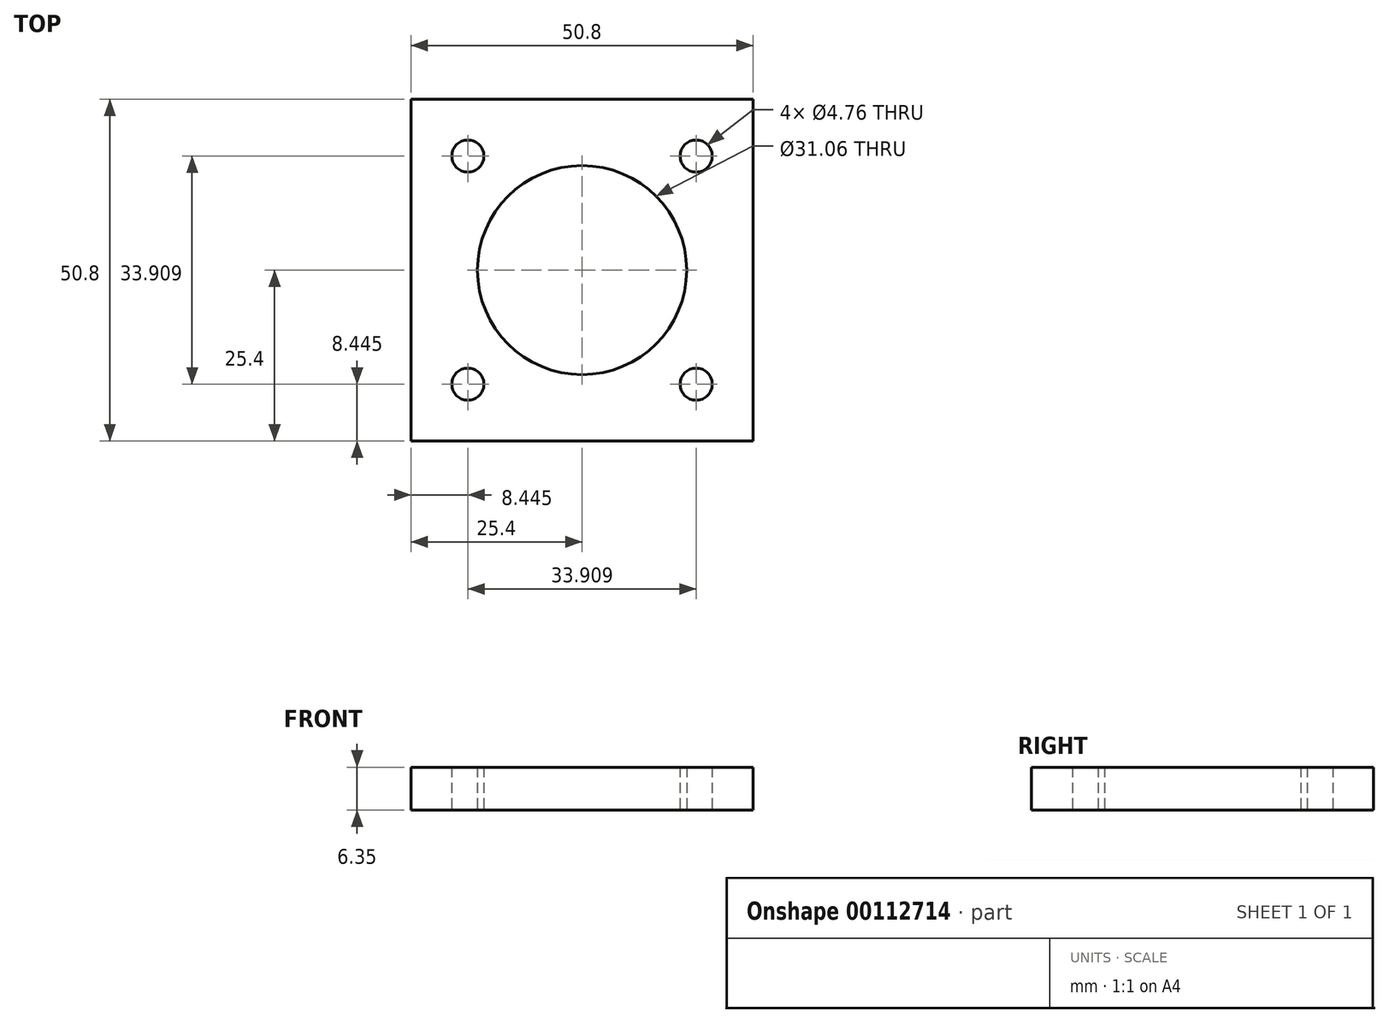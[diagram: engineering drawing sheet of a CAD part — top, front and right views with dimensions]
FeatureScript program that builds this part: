
annotation { "Feature Type Name" : "Feature", "Feature Type Description" : "" }
export const myFeature = defineFeature(function(context is Context, id is Id, definition is map)
    precondition{}
    {
        {
            var Q0;
            Q0=qCreatedBy(makeId("Top.planeOp"),FACE);
            var sketch = newSketch(context, id + "F0", { "sketchPlane" : qUnion([Q0])});
            skLineSegment(sketch, "E0.bottom", {"start": v(25.4, -25.4) * mm, "end": v(-25.4, -25.4) * mm});
            skLineSegment(sketch, "E0.top", {"start": v(25.4, 25.4) * mm, "end": v(-25.4, 25.4) * mm});
            skLineSegment(sketch, "E0.left", {"start": v(25.4, -25.4) * mm, "end": v(25.4, 25.4) * mm});
            skLineSegment(sketch, "E0.right", {"start": v(-25.4, -25.4) * mm, "end": v(-25.4, 25.4) * mm});
            skPoint(sketch, "E0.middle", {"position": v(0, 0) * mm});
            skLineSegment(sketch, "E1.bottom", {"start": v(16.95, 16.95) * mm, "end": v(-16.95, 16.95) * mm, "construction": true});
            skLineSegment(sketch, "E1.top", {"start": v(16.95, -16.95) * mm, "end": v(-16.95, -16.95) * mm, "construction": true});
            skLineSegment(sketch, "E1.left", {"start": v(16.95, 16.95) * mm, "end": v(16.95, -16.95) * mm, "construction": true});
            skLineSegment(sketch, "E1.right", {"start": v(-16.95, 16.95) * mm, "end": v(-16.95, -16.95) * mm, "construction": true});
            skCircle(sketch, "E2", {"center": v(0, 0) * mm, "radius": 15.53 * mm});
            skCircle(sketch, "E3", {"center": v(-16.95, 16.95) * mm, "radius": 8.45 * mm, "construction": true});
            skCircle(sketch, "E4", {"center": v(-16.95, 16.95) * mm, "radius": 2.38 * mm});
            skCircle(sketch, "E5", {"center": v(16.95, 16.95) * mm, "radius": 2.38 * mm});
            skCircle(sketch, "E6", {"center": v(-16.95, -16.95) * mm, "radius": 2.38 * mm});
            skCircle(sketch, "E7", {"center": v(16.95, -16.95) * mm, "radius": 2.38 * mm});
            skSolve(sketch);
        }
        {
            var Q0;
            Q0=qSketchRegion(id+"F0",true);
            extrude(context, id + "F1", {"entities" : qUnion([Q0]), "depth" : 6.35 * mm});
        }
    });
